# Revit family: Tankless_Water_Heater-Keltech-CNA_Series
name_source: partatom
category: Plumbing Fixtures
revit_build: Autodesk Revit Architecture 2012 (Build: 20110916_2132(x64)
units: mm (PartAtom-declared; Revit-internal decimal feet)

## types (14) — shared parameters
Actual Chilled Water Flow = 0 GPM
Actual Heating Water Flow = 0 GPM
Apparent Load = 0 VA
Assembly Code = D2020200
Buy American Act = To Be Determined
CTRL Inlet Top Inset = 31.5 "
CTRL Width = 30 "
Cold Water Connector Description = Cold Water
Cold Water Inlet = 1"
Cold Water Inlet Radius = 0.5 "
Depth = 12.692 "
Electrical Connector Description = Power
Electrical Connector Right Inset = 3 "
Electrical Connector Top Inset = 22 "
Hot Water Connector Description = Hot Water
Hot Water Outlet Diameter = 1"
Hot Water Outlet Radius = 0.5 "
Housing Material = Metal - Bradley Corp - Grey - Painted
Industry Standards = CSA
Inlet Back Offset = 3.75 "
Inlet Top Inset = 31.5 "
Manufacturer = Keltech Inc. a Subsidiary of Bradley Corp
MasterFormat Number = 22.45.26
MasterFormat Title = Instantaneous Electric Domestic Water Heaters
Number of Poles = 1
Outlet Right Inset = 23.5 "
PTFE Coating TE2 = No
Phase = 3
Pipe Material = Metal - Bradley Corp - Copper
Product Tech Data URL - English = http://www.keltech-inc.com
Specifications URL = http://www.keltech-inc.com
URL = http://www.bradleycorp.com
Version = 1.0
Warranty Information = One Year
Width = 30 "
zero-valued in all types: Power Factor

## per-type parameters (varying)
| type | CTRL Cabinet Height | Cabinet Height | Current | Description | Length | Voltage | Wattage |
| CNA-363/480D | 48 " | 48 " | 43 A | Three Phase 36 kW, 480V | 60 " | 480 V | 36000 W |
| CNA-363/600D | 48 " | 48 " | 35 A | Three Phase 36 kW, 600V | 60 " | 600 V | 36000 W |
| CNA-543/480D | 48 " | 48 " | 65 A | Three Phase 54 kW, 480V | 60 " | 480 V | 54000 W |
| CNA-543/600D | 48 " | 48 " | 52 A | Three Phase 54 kW, 600V | 60 " | 600 V | 54000 W |
| CNA-633/480D | 60 " | 60 " | 76 A | Three Phase 63 kW, 480V | 72 " | 480 V | 63000 W |
| CNA-633/600D | 60 " | 60 " | 61 A | Three Phase 63 kW, 600V | 72 " | 600 V | 63000 W |
| CNA-723/480D | 48 " | 48 " | 87 A | Three Phase 72 kW, 480V | 60 " | 480 V | 72000 W |
| CNA-723/600D | 48 " | 48 " | 69 A | Three Phase 72 kW, 600V | 60 " | 600 V | 72000 W |
| CNA-1083/480D | 48 " | 48 " | 132 A | Three Phase 108 kW, 480V | 60 " | 480 V | 108000 W |
| CNA-1083/600D | 48 " | 48 " | 104 A | Three Phase 108 kW, 600V | 60 " | 600 V | 108000 W |
| CNA-1263/480D | 60 " | 60 " | 152 A | Three Phase 126 kW, 480V | 72 " | 480 V | 126000 W |
| CNA-1263/600D | 60 " | 60 " | 121 A | Three Phase 126 kW, 600V | 72 " | 600 V | 126000 W |
| CNA-1443/480D | 60 " | 60 " | 174 A | Three Phase 144 kW, 480V | 72 " | 480 V | 144000 W |
| CNA-1443/600D | 60 " | 60 " | 139 A | Three Phase 144 kW, 600V | 72 " | 600 V | 144000 W |

note: column(s) folded — value = type name in every type: Model

## geometry (parser evidence)
native form markers: Blend x8, Sweep x2
no freeform markers — native parametric forms only
